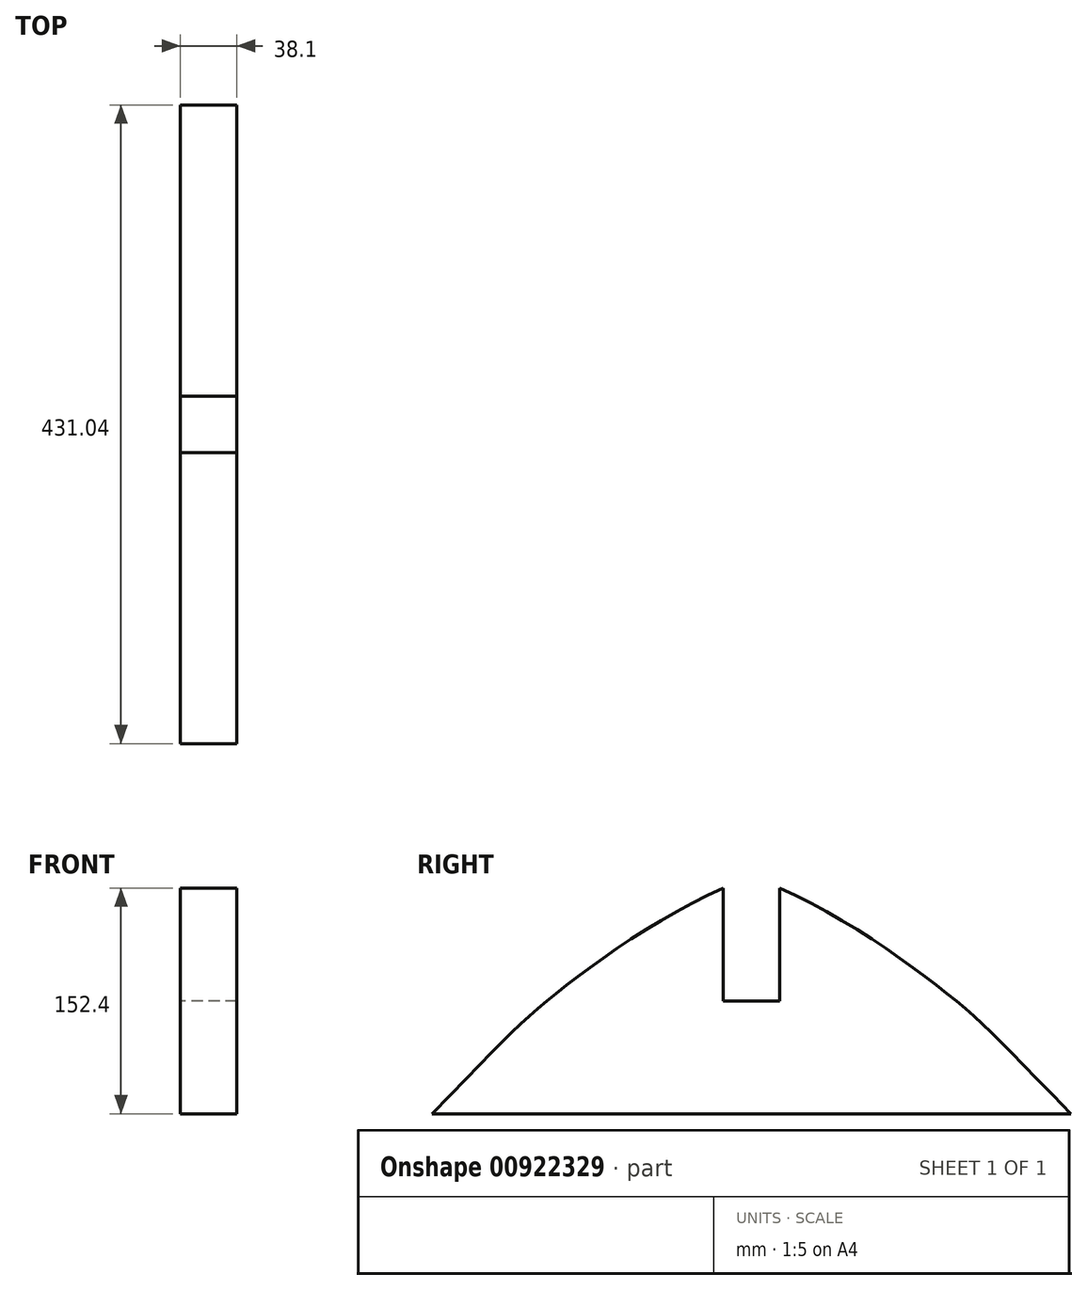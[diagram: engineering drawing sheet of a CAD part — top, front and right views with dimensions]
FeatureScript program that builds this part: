
annotation { "Feature Type Name" : "Feature", "Feature Type Description" : "" }
export const myFeature = defineFeature(function(context is Context, id is Id, definition is map)
    precondition{}
    {
        {
            var Q0;
            Q0=qCreatedBy(makeId("Right.planeOp"),FACE);
            var sketch = newSketch(context, id + "F0", { "sketchPlane" : qUnion([Q0])});
            skFitSpline(sketch, "E0", {"points": [v(-132.43, 0) * mm, v(-47.5, 82.2) * mm, v(64.04, 152.4) * mm], "startDerivative": vector(299.43, 308.27) * mm, "endDerivative": vector(242.08, 105.86) * mm});
            skLineSegment(sketch, "E1", {"start": v(-132.43, 0) * mm, "end": v(83.09, 0) * mm});
            skLineSegment(sketch, "E2", {"start": v(64.04, 152.4) * mm, "end": v(64.04, 76.12) * mm});
            skLineSegment(sketch, "E3", {"start": v(64.04, 76.12) * mm, "end": v(83.09, 76.12) * mm});
            skFitSpline(sketch, "E4.MirrorCS", {"points": [v(298.6, 0) * mm, v(213.67, 82.2) * mm, v(102.14, 152.4) * mm], "startDerivative": vector(-299.43, 308.27) * mm, "endDerivative": vector(-242.08, 105.86) * mm});
            skLineSegment(sketch, "E5.MirrorCS", {"start": v(102.14, 76.12) * mm, "end": v(83.09, 76.12) * mm});
            skLineSegment(sketch, "E6.MirrorCS", {"start": v(298.6, 0) * mm, "end": v(83.09, 0) * mm});
            skLineSegment(sketch, "E7.MirrorCS", {"start": v(102.14, 152.4) * mm, "end": v(102.14, 76.12) * mm});
            skSolve(sketch);
        }
        {
            var Q0;
            Q0=makeQuery(id+"F0.imprint","IMPRINT",FACE,{"disambiguationData":[TD([[makeQuery(id+"F0.imprint","IMPRINT",EDGE,{"derivedFrom":sQuery(id+"F0.wireOp",EDGE,"E0")}),-1.0]])]});
            extrude(context, id + "F1", {"entities" : qUnion([Q0]), "depth" : 38.1 * mm, "offsetDistance" : 25.4 * mm});
        }
    });
